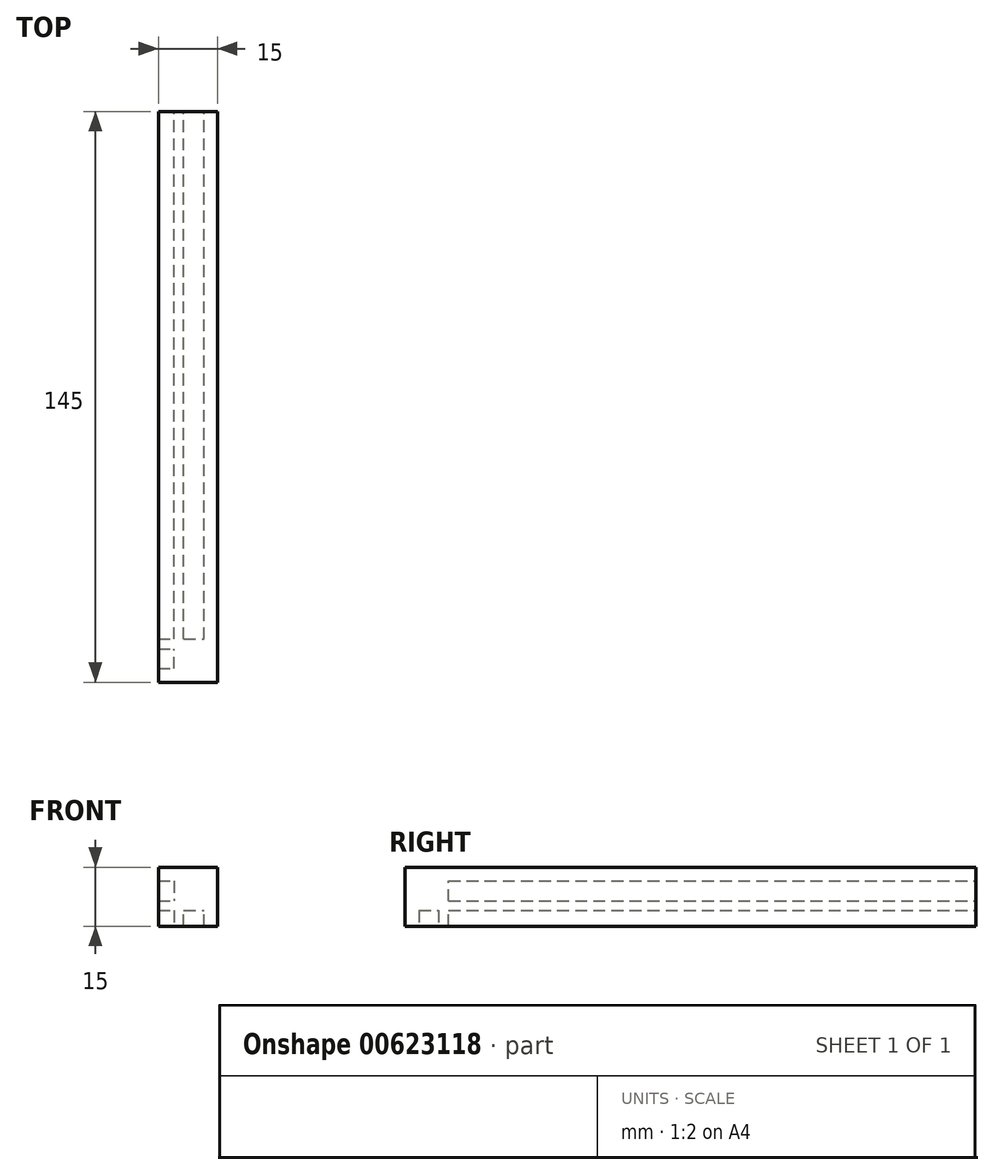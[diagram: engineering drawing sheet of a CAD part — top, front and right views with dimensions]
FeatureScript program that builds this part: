
annotation { "Feature Type Name" : "Feature", "Feature Type Description" : "" }
export const myFeature = defineFeature(function(context is Context, id is Id, definition is map)
    precondition{}
    {
        {
            var Q0;
            Q0=qCreatedBy(makeId("Front.planeOp"),FACE);
            var sketch = newSketch(context, id + "F0", { "sketchPlane" : qUnion([Q0])});
            skLineSegment(sketch, "E0.bottom", {"start": v(0, 0) * mm, "end": v(15, 0) * mm});
            skLineSegment(sketch, "E0.top", {"start": v(0, 15) * mm, "end": v(15, 15) * mm});
            skLineSegment(sketch, "E0.left", {"start": v(0, 0) * mm, "end": v(0, 15) * mm});
            skLineSegment(sketch, "E0.right", {"start": v(15, 0) * mm, "end": v(15, 15) * mm});
            skLineSegment(sketch, "E1.bottom", {"start": v(6.45, 0) * mm, "end": v(11.55, 0) * mm});
            skLineSegment(sketch, "E1.top", {"start": v(6.45, 4) * mm, "end": v(11.55, 4) * mm});
            skLineSegment(sketch, "E1.left", {"start": v(6.45, 0) * mm, "end": v(6.45, 4) * mm});
            skLineSegment(sketch, "E1.right", {"start": v(11.55, 0) * mm, "end": v(11.55, 4) * mm});
            skLineSegment(sketch, "E2.bottom", {"start": v(0, 11.55) * mm, "end": v(4, 11.55) * mm});
            skLineSegment(sketch, "E2.top", {"start": v(0, 6.45) * mm, "end": v(4, 6.45) * mm});
            skLineSegment(sketch, "E2.left", {"start": v(0, 11.55) * mm, "end": v(0, 6.45) * mm});
            skLineSegment(sketch, "E2.right", {"start": v(4, 11.55) * mm, "end": v(4, 6.45) * mm});
            skLineSegment(sketch, "E3", {"start": v(0, 9) * mm, "end": v(9.14, 9) * mm, "construction": true});
            skLineSegment(sketch, "E4", {"start": v(9, 0) * mm, "end": v(9, 6.55) * mm, "construction": true});
            skSolve(sketch);
        }
        {
            var Q0;
            {var subQ5=sQuery(id+"F0.wireOp",EDGE,"E0.top");Q0=makeQuery(id+"F0.imprint","IMPRINT",FACE,{"disambiguationData":[TD([[makeQuery(id+"F0.imprint","IMPRINT",EDGE,{"derivedFrom":subQ5}),-1.0]])]});}
            extrude(context, id + "F1", {"entities" : qUnion([Q0]), "depth" : 138 * mm, "offsetDistance" : 25 * mm});
        }
        {
            var Q0;
            Q0=makeQuery(id+"F1.opExtrude","CAP_FACE",FACE,{"disambiguationData":[OSD([sQuery(id+"F0.wireOp",EDGE,"E0.bottom"),sQuery(id+"F0.wireOp",EDGE,"E0.top"),sQuery(id+"F0.wireOp",EDGE,"E0.left"),sQuery(id+"F0.wireOp",EDGE,"E0.right"),sQuery(id+"F0.wireOp",EDGE,"E1.top"),sQuery(id+"F0.wireOp",EDGE,"E1.left"),sQuery(id+"F0.wireOp",EDGE,"E1.right"),sQuery(id+"F0.wireOp",EDGE,"E2.bottom"),sQuery(id+"F0.wireOp",EDGE,"E2.top"),sQuery(id+"F0.wireOp",EDGE,"E2.right")])],"isStart":false});
            var sketch = newSketch(context, id + "F2", { "sketchPlane" : qUnion([Q0])});
            skLineSegment(sketch, "E5.bottom", {"start": v(0, 0) * mm, "end": v(15, 0) * mm});
            skLineSegment(sketch, "E5.top", {"start": v(0, 15) * mm, "end": v(15, 15) * mm});
            skLineSegment(sketch, "E5.left", {"start": v(0, 0) * mm, "end": v(0, 15) * mm});
            skLineSegment(sketch, "E5.right", {"start": v(15, 0) * mm, "end": v(15, 15) * mm});
            skSolve(sketch);
        }
        {
            var Q0;
            Q0 = qSketchRegion(id + "F2", true);
            extrude(context, id + "F3", {"entities" : qUnion([Q0]), "operationType" : NewBodyOperationType.ADD, "depth" : 7 * mm, "offsetDistance" : 25 * mm, "hasSecondDirection" : true, "secondDirectionOppositeDirection" : true, "secondDirectionDepth" : 4 * mm});
        }
        {
            var Q0;
            {var subQ0=sQuery(id+"F0.wireOp",EDGE,"E0.bottom");Q0=makeQuery(id+"F3.boolean.opBoolean","MERGE",FACE,{"derivedFrom":[makeQuery(id+"F1.opExtrude","SWEPT_FACE",FACE,{"disambiguationData":[OSD([subQ0]),TDD([makeQuery(id+"F0.imprint","IMPRINT",EDGE,{"disambiguationData":[TD([[makeQuery(id+"F0.imprint","INTERSECT",VERTEX,{"derivedFrom":[subQ0,sQuery(id+"F0.wireOp",EDGE,"E0.left")]}),-1.0]])],"derivedFrom":subQ0})])]}),makeQuery(id+"F1.opExtrude","SWEPT_FACE",FACE,{"disambiguationData":[OSD([subQ0]),TDD([makeQuery(id+"F0.imprint","IMPRINT",EDGE,{"disambiguationData":[TD([[makeQuery(id+"F0.imprint","INTERSECT",VERTEX,{"derivedFrom":[subQ0,sQuery(id+"F0.wireOp",EDGE,"E0.right")]}),1.0]])],"derivedFrom":subQ0})])]}),makeQuery(id+"F3.opExtrude","SWEPT_FACE",FACE,{"disambiguationData":[OSD([sQuery(id+"F2.wireOp",EDGE,"E5.bottom")])]})]});}
            var sketch = newSketch(context, id + "F4", { "sketchPlane" : qUnion([Q0])});
            skLineSegment(sketch, "E6.bottom", {"start": v(0, 141.5) * mm, "end": v(4, 141.5) * mm});
            skLineSegment(sketch, "E6.top", {"start": v(0, 136.5) * mm, "end": v(4, 136.5) * mm});
            skLineSegment(sketch, "E6.left", {"start": v(0, 141.5) * mm, "end": v(0, 136.5) * mm});
            skLineSegment(sketch, "E6.right", {"start": v(4, 141.5) * mm, "end": v(4, 136.5) * mm});
            skSolve(sketch);
        }
        {
            var Q0;
            Q0 = qSketchRegion(id + "F4", true);
            extrude(context, id + "F5", {"entities" : qUnion([Q0]), "operationType" : NewBodyOperationType.REMOVE, "oppositeDirection" : true, "depth" : 4 * mm, "offsetDistance" : 25 * mm});
        }
    });
